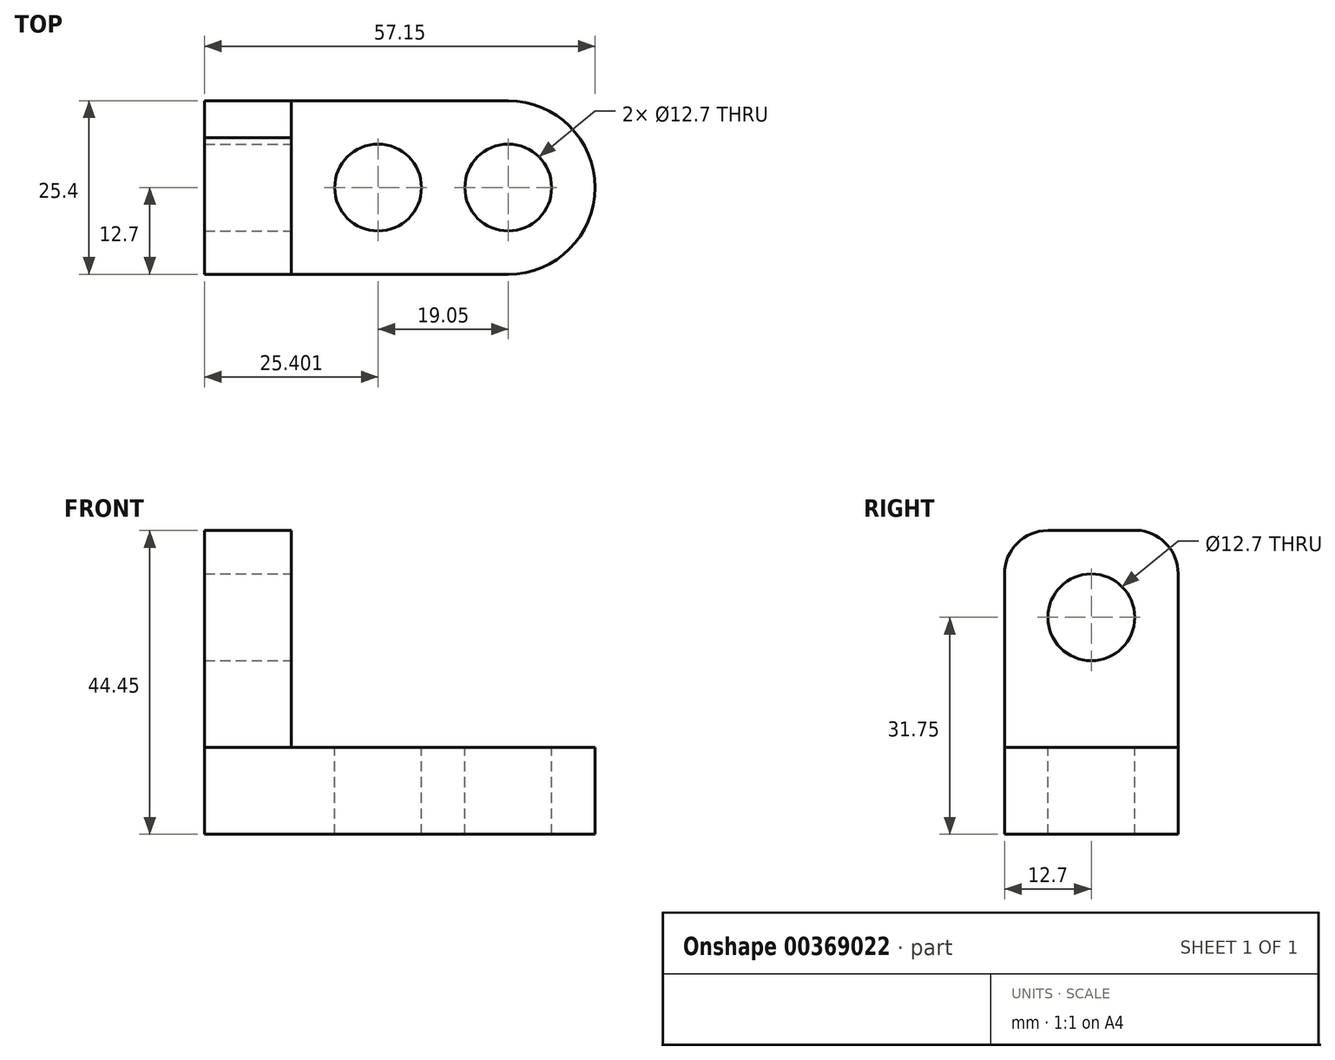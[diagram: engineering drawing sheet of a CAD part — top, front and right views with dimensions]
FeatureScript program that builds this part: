
annotation { "Feature Type Name" : "Feature", "Feature Type Description" : "" }
export const myFeature = defineFeature(function(context is Context, id is Id, definition is map)
    precondition{}
    {
        {
            var Q0;
            Q0=qCreatedBy(makeId("Front.planeOp"),FACE);
            var sketch = newSketch(context, id + "F0", { "sketchPlane" : qUnion([Q0])});
            skLineSegment(sketch, "E0", {"start": v(-36.69, 0) * mm, "end": v(-36.69, 12.7) * mm});
            skLineSegment(sketch, "E1", {"start": v(-36.69, 12.7) * mm, "end": v(20.46, 12.7) * mm});
            skLineSegment(sketch, "E2", {"start": v(20.46, 12.7) * mm, "end": v(20.46, 0) * mm});
            skLineSegment(sketch, "E3", {"start": v(20.46, 0) * mm, "end": v(-36.69, 0) * mm});
            skSolve(sketch);
        }
        {
            var Q0;
            Q0=makeQuery(id+"F0.imprint","IMPRINT",FACE,{"disambiguationData":[TD([[makeQuery(id+"F0.imprint","IMPRINT",EDGE,{"derivedFrom":sQuery(id+"F0.wireOp",EDGE,"E0")}),-1.0]])]});
            extrude(context, id + "F1", {"entities" : qUnion([Q0]), "depth" : 25.4 * mm});
        }
        {
            var Q0;
            Q0=makeQuery(id+"F1.opExtrude","SWEPT_FACE",FACE,{"disambiguationData":[OSD([sQuery(id+"F0.wireOp",EDGE,"E1")])]});
            var sketch = newSketch(context, id + "F2", { "sketchPlane" : qUnion([Q0])});
            skLineSegment(sketch, "E4", {"start": v(-36.69, 0) * mm, "end": v(-23.99, 0) * mm});
            skLineSegment(sketch, "E5", {"start": v(-23.99, 0) * mm, "end": v(-23.99, -25.4) * mm});
            skLineSegment(sketch, "E6", {"start": v(-23.99, -25.4) * mm, "end": v(-36.69, -25.4) * mm});
            skLineSegment(sketch, "E7", {"start": v(-36.69, -25.4) * mm, "end": v(-36.69, 0) * mm});
            skSolve(sketch);
        }
        {
            var Q0;
            Q0=makeQuery(id+"F2.imprint","IMPRINT",FACE,{"disambiguationData":[TD([[makeQuery(id+"F2.imprint","IMPRINT",EDGE,{"derivedFrom":sQuery(id+"F2.wireOp",EDGE,"E4")}),-1.0]])]});
            extrude(context, id + "F3", {"entities" : qUnion([Q0]), "depth" : 31.75 * mm});
        }
        {
            var Q0;
            Q0=makeQuery(id+"F3.opExtrude","SWEPT_FACE",FACE,{"disambiguationData":[OSD([sQuery(id+"F2.wireOp",EDGE,"E5")])]});
            var sketch = newSketch(context, id + "F4", { "sketchPlane" : qUnion([Q0])});
            skCircle(sketch, "E8", {"center": v(-12.7, 31.75) * mm, "radius": 6.35 * mm});
            skPoint(sketch, "E8.centerSnap0", {"position": v(-12.7, 44.45) * mm});
            skLineSegment(sketch, "E9", {"start": v(-19.05, 31.75) * mm, "end": v(-19.05, 44.45) * mm});
            skLineSegment(sketch, "E10", {"start": v(-19.05, 44.45) * mm, "end": v(-19.05, 31.75) * mm});
            skLineSegment(sketch, "E11", {"start": v(-19.05, 31.75) * mm, "end": v(-6.35, 31.75) * mm});
            skLineSegment(sketch, "E12", {"start": v(-6.35, 31.75) * mm, "end": v(-6.35, 44.45) * mm});
            skLineSegment(sketch, "E13", {"start": v(-6.35, 44.45) * mm, "end": v(-19.05, 44.45) * mm});
            skSolve(sketch);
        }
        {
            var Q0;
            {var subQ1=sQuery(id+"F4.wireOp",EDGE,"E10");Q0=makeQuery(id+"F4.imprint","IMPRINT",FACE,{"disambiguationData":[TD([[makeQuery(id+"F4.imprint","IMPRINT",EDGE,{"derivedFrom":subQ1}),1.0]])]});}
            var Q1;
            {var subQ0=sQuery(id+"F4.wireOp",EDGE,"E11");Q1=makeQuery(id+"F4.imprint","IMPRINT",FACE,{"disambiguationData":[TD([[makeQuery(id+"F4.imprint","IMPRINT",EDGE,{"derivedFrom":subQ0}),1.0]])]});}
            var Q2;
            {var subQ0=sQuery(id+"F4.wireOp",EDGE,"E11");Q2=makeQuery(id+"F4.imprint","IMPRINT",FACE,{"disambiguationData":[TD([[makeQuery(id+"F4.imprint","IMPRINT",EDGE,{"derivedFrom":subQ0}),-1.0]])]});}
            extrude(context, id + "F5", {"entities" : qUnion([Q0, Q1, Q2]), "operationType" : NewBodyOperationType.REMOVE, "oppositeDirection" : true, "depth" : 25.4 * mm});
        }
        {
            var Q0;
            Q0=makeQuery(id+"F3.opExtrude","SWEPT_FACE",FACE,{"disambiguationData":[OSD([sQuery(id+"F2.wireOp",EDGE,"E5")])]});
            var sketch = newSketch(context, id + "F6", { "sketchPlane" : qUnion([Q0])});
            skLineSegment(sketch, "E14", {"start": v(-19.05, 44.45) * mm, "end": v(-19.05, 44.45) * mm});
            skLineSegment(sketch, "E15", {"start": v(-25.4, 38.1) * mm, "end": v(-25.4, 12.7) * mm});
            skPoint(sketch, "E16.visualSharp", {"position": v(-25.4, 44.45) * mm});
            skArc(sketch, "E16.filletArc", {"start": v(-19.05, 44.45) * mm, "mid": v(-23.54, 42.6) * mm, "end": v(-25.4, 38.1) * mm});
            skSolve(sketch);
        }
        {
            var Q0;
            Q0=makeQuery(id+"F6.imprint","IMPRINT",FACE,{"disambiguationData":[TD([[makeQuery(id+"F6.imprint","IMPRINT",EDGE,{"derivedFrom":sQuery(id+"F6.wireOp",EDGE,"E15")}),1.0]])]});
            var sketch = newSketch(context, id + "F7", { "sketchPlane" : qUnion([Q0])});
            skLineSegment(sketch, "E17", {"start": v(-6.39, 44.52) * mm, "end": v(-6.35, 44.52) * mm});
            skLineSegment(sketch, "E18", {"start": v(0, 38.17) * mm, "end": v(0, 12.87) * mm});
            skPoint(sketch, "E19.visualSharp", {"position": v(0, 44.52) * mm});
            skArc(sketch, "E19.filletArc", {"start": v(0, 38.17) * mm, "mid": v(-1.86, 42.66) * mm, "end": v(-6.35, 44.52) * mm});
            skSolve(sketch);
        }
        {
            var Q0;
            {var subQ0=sQuery(id+"F6.wireOp",EDGE,"E16.filletArc");Q0=makeQuery(id+"F6.imprint","IMPRINT",FACE,{"disambiguationData":[TD([[makeQuery(id+"F6.imprint","IMPRINT",EDGE,{"derivedFrom":subQ0}),-1.0]])]});}
            extrude(context, id + "F8", {"entities" : qUnion([Q0]), "operationType" : NewBodyOperationType.REMOVE, "oppositeDirection" : true, "depth" : 25.4 * mm});
        }
        {
            var Q0;
            {var subQ0=sQuery(id+"F7.wireOp",EDGE,"E19.filletArc");var subQ1=sQuery(id+"F2.wireOp",EDGE,"E5");var subQ2=sQuery(id+"F2.wireOp",EDGE,"E4");var subQ3=makeQuery(id+"F6.imprint","IMPRINT",EDGE,{"derivedFrom":makeQuery(id+"F3.opExtrude","SWEPT_EDGE",EDGE,{"disambiguationData":[OSD([sQuery(id+"F0.wireOp",EDGE,"E1"),subQ2,subQ1])]})});var subQ4=makeQuery(id+"F7.imprint","INTERSECT",VERTEX,{"derivedFrom":[subQ3,sQuery(id+"F7.wireOp",EDGE,"E18"),subQ0]});Q0=makeQuery(id+"F7.imprint","IMPRINT",FACE,{"disambiguationData":[TD([[makeQuery(id+"F7.imprint","IMPRINT",EDGE,{"disambiguationData":[TD([[subQ4,-1.0]])],"derivedFrom":subQ0}),-1.0]])]});}
            extrude(context, id + "F9", {"entities" : qUnion([Q0]), "operationType" : NewBodyOperationType.REMOVE, "oppositeDirection" : true, "depth" : 25.4 * mm});
        }
        {
            var Q0;
            Q0=makeQuery(id+"F1.opExtrude","SWEPT_FACE",FACE,{"disambiguationData":[OSD([sQuery(id+"F0.wireOp",EDGE,"E1")])]});
            var sketch = newSketch(context, id + "F10", { "sketchPlane" : qUnion([Q0])});
            skCircle(sketch, "E20", {"center": v(7.76, -12.7) * mm, "radius": 6.35 * mm});
            skPoint(sketch, "E20.centerSnap0", {"position": v(20.46, -12.7) * mm});
            skCircle(sketch, "E21", {"center": v(-11.29, -12.7) * mm, "radius": 6.35 * mm});
            skSolve(sketch);
        }
        {
            var Q0;
            Q0=makeQuery(id+"F10.imprint","IMPRINT",FACE,{"disambiguationData":[TD([[makeQuery(id+"F10.imprint","IMPRINT",EDGE,{"derivedFrom":sQuery(id+"F10.wireOp",EDGE,"E21")}),1.0]])]});
            var Q1;
            Q1=makeQuery(id+"F10.imprint","IMPRINT",FACE,{"disambiguationData":[TD([[makeQuery(id+"F10.imprint","IMPRINT",EDGE,{"derivedFrom":sQuery(id+"F10.wireOp",EDGE,"E20")}),1.0]])]});
            extrude(context, id + "F11", {"entities" : qUnion([Q0, Q1]), "operationType" : NewBodyOperationType.REMOVE, "oppositeDirection" : true, "depth" : 25.4 * mm});
        }
        {
            var Q0;
            Q0=makeQuery(id+"F1.opExtrude","SWEPT_FACE",FACE,{"disambiguationData":[OSD([sQuery(id+"F0.wireOp",EDGE,"E1")])]});
            var sketch = newSketch(context, id + "F12", { "sketchPlane" : qUnion([Q0])});
            skPoint(sketch, "E22", {"position": v(20.46, -12.7) * mm});
            skPoint(sketch, "E23", {"position": v(7.76, -12.7) * mm});
            skPoint(sketch, "E24", {"position": v(7.76, -25.4) * mm});
            skPoint(sketch, "E25", {"position": v(7.76, 0) * mm});
            skArc(sketch, "E26", {"start": v(7.76, -25.4) * mm, "mid": v(16.74, -21.68) * mm, "end": v(20.46, -12.7) * mm});
            skArc(sketch, "E27", {"start": v(20.46, -12.7) * mm, "mid": v(16.74, -3.72) * mm, "end": v(7.76, 0) * mm});
            skSolve(sketch);
        }
        {
            var Q0;
            {var subQ0=sQuery(id+"F12.wireOp",EDGE,"E26");Q0=makeQuery(id+"F12.imprint","IMPRINT",FACE,{"disambiguationData":[TD([[makeQuery(id+"F12.imprint","IMPRINT",EDGE,{"derivedFrom":subQ0}),-1.0]])]});}
            var Q1;
            {var subQ0=sQuery(id+"F12.wireOp",EDGE,"E27");Q1=makeQuery(id+"F12.imprint","IMPRINT",FACE,{"disambiguationData":[TD([[makeQuery(id+"F12.imprint","IMPRINT",EDGE,{"derivedFrom":subQ0}),-1.0]])]});}
            extrude(context, id + "F13", {"entities" : qUnion([Q0, Q1]), "operationType" : NewBodyOperationType.REMOVE, "oppositeDirection" : true, "depth" : 25.4 * mm});
        }
    });
